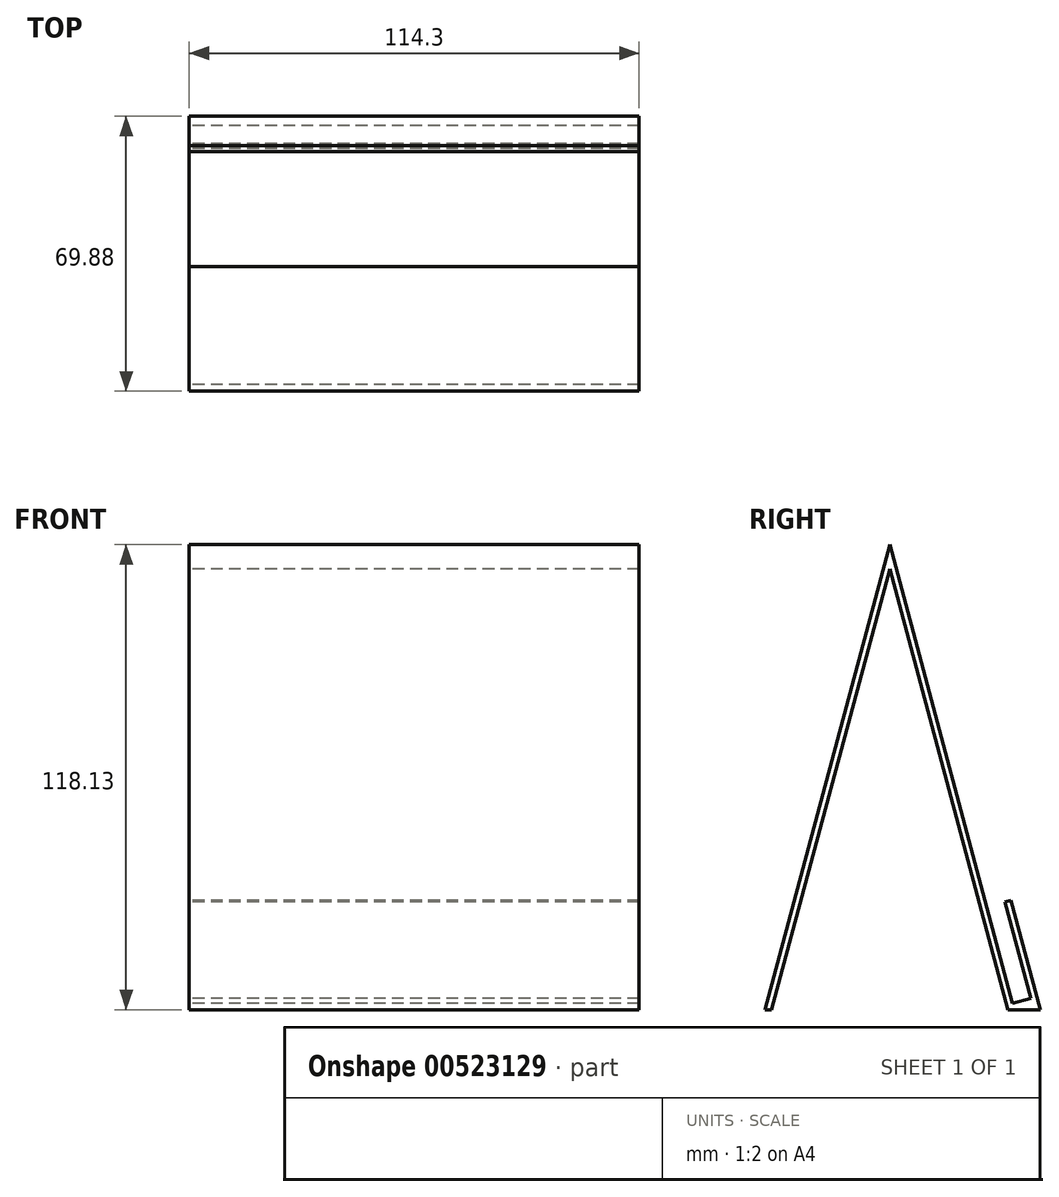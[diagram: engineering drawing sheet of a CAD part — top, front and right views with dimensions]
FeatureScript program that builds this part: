
annotation { "Feature Type Name" : "Feature", "Feature Type Description" : "" }
export const myFeature = defineFeature(function(context is Context, id is Id, definition is map)
    precondition{}
    {
        {
            var Q0;
            Q0=qCreatedBy(makeId("Right.planeOp"),FACE);
            var sketch = newSketch(context, id + "F0", { "sketchPlane" : qUnion([Q0])});
            skLineSegment(sketch, "E0", {"start": v(0, 0) * mm, "end": v(-30, 112) * mm});
            skLineSegment(sketch, "E1", {"start": v(-30, 112) * mm, "end": v(-60.02, 0) * mm});
            skLineSegment(sketch, "E2", {"start": v(-30, 112) * mm, "end": v(-30, 0) * mm, "construction": true});
            skLineSegment(sketch, "E3", {"start": v(0, 0) * mm, "end": v(8.22, 0) * mm});
            skLineSegment(sketch, "E4", {"start": v(8.22, 0) * mm, "end": v(0.78, 27.77) * mm});
            skLineSegment(sketch, "E5", {"start": v(0.78, 27.77) * mm, "end": v(-0.76, 27.35) * mm});
            skLineSegment(sketch, "E6", {"start": v(-0.76, 27.35) * mm, "end": v(5.82, 2.82) * mm});
            skLineSegment(sketch, "E7", {"start": v(5.82, 2.82) * mm, "end": v(1.22, 1.59) * mm});
            skLineSegment(sketch, "E8", {"start": v(1.22, 1.59) * mm, "end": v(-30, 118.13) * mm});
            skLineSegment(sketch, "E9", {"start": v(-30, 118.13) * mm, "end": v(-61.66, 0) * mm});
            skLineSegment(sketch, "E10", {"start": v(-61.66, 0) * mm, "end": v(-60.02, 0) * mm});
            skSolve(sketch);
        }
        {
            var Q0;
            Q0 = qSketchRegion(id + "F0", true);
            extrude(context, id + "F1", {"entities" : qUnion([Q0]), "depth" : 114.3 * mm, "offsetDistance" : 25.4 * mm});
        }
    });
